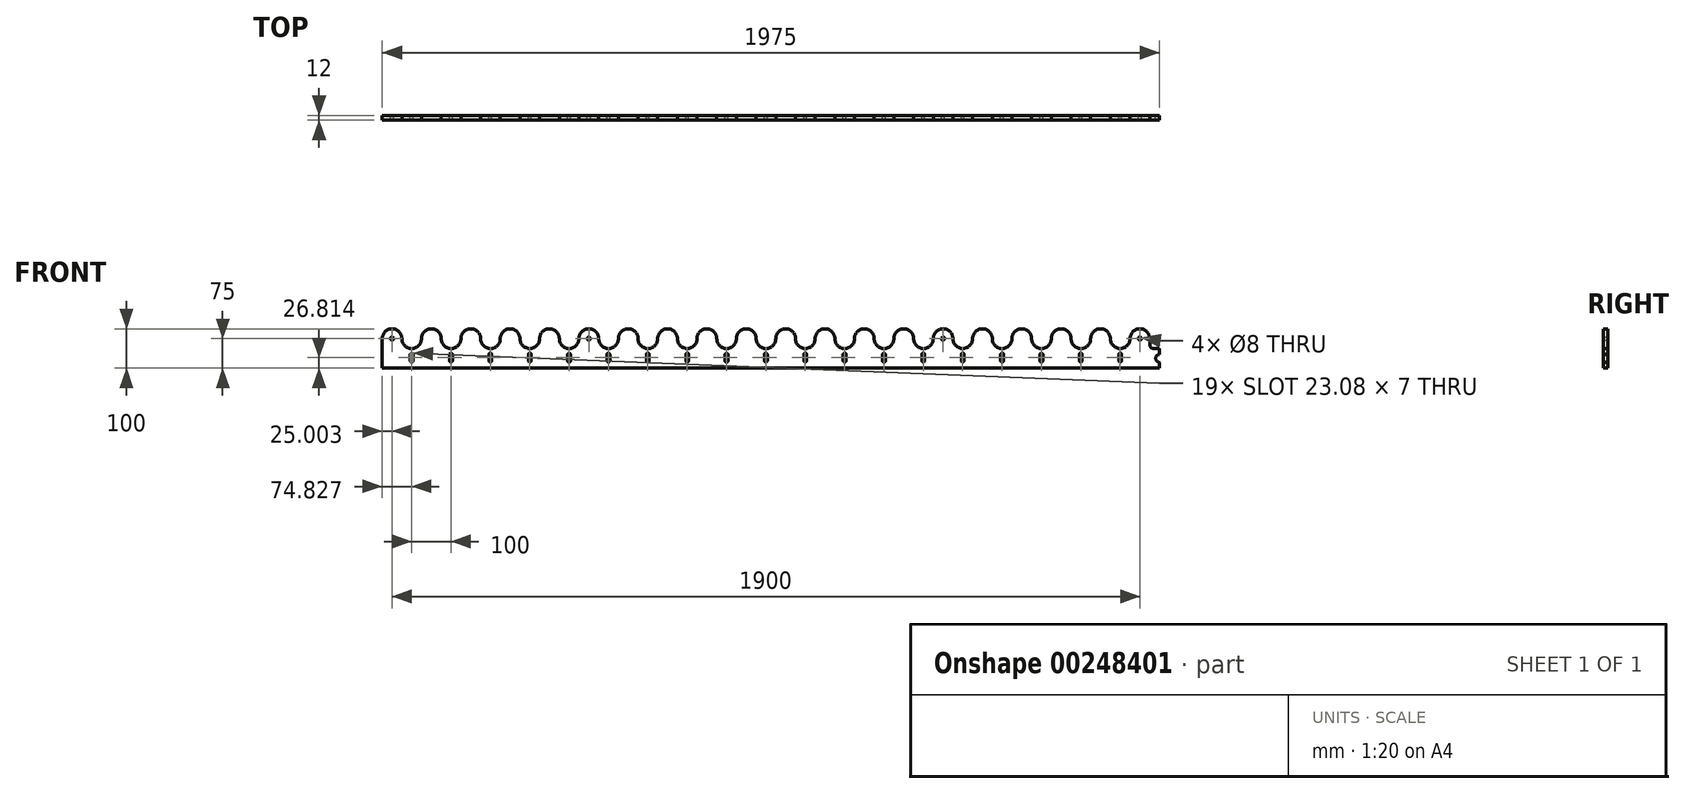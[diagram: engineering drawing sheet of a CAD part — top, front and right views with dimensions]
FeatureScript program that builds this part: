
annotation { "Feature Type Name" : "Feature", "Feature Type Description" : "" }
export const myFeature = defineFeature(function(context is Context, id is Id, definition is map)
    precondition{}
    {
        {
            var Q0;
            Q0=qCreatedBy(makeId("Front.planeOp"),FACE);
            var sketch = newSketch(context, id + "F0", { "sketchPlane" : qUnion([Q0])});
            skArc(sketch, "E0", {"start": v(19.37, 31.06) * mm, "mid": v(15.85, 34.56) * mm, "end": v(12.37, 31.03) * mm});
            skLineSegment(sketch, "E1", {"start": v(12.37, 31.03) * mm, "end": v(12.37, 14.95) * mm});
            skLineSegment(sketch, "E2", {"start": v(19.37, 31.06) * mm, "end": v(19.37, 14.98) * mm});
            skArc(sketch, "E3", {"start": v(19.37, 14.98) * mm, "mid": v(15.89, 11.48) * mm, "end": v(12.37, 14.95) * mm});
            skLineSegment(sketch, "E4.direction1", {"start": v(-61.28, 71.21) * mm, "end": v(88.44, 71.21) * mm, "construction": true});
            skLineSegment(sketch, "E5", {"start": v(-62.08, 71.21) * mm, "end": v(-78.8, 71.21) * mm, "construction": true});
            skLineSegment(sketch, "E6", {"start": v(15.87, 14.98) * mm, "end": v(16.2, 118.2) * mm, "construction": true});
            skArc(sketch, "E7", {"start": v(41.04, 71.21) * mm, "mid": v(16.04, 46.21) * mm, "end": v(-8.96, 71.21) * mm});
            skPoint(sketch, "E7.centerSnap0", {"position": v(13.58, 71.21) * mm});
            skArc(sketch, "E8", {"start": v(-8.96, 71.21) * mm, "mid": v(-33.96, 96.21) * mm, "end": v(-58.96, 71.21) * mm});
            skArc(sketch, "E9.1.0.0", {"start": v(91.04, 71.21) * mm, "mid": v(66.04, 96.21) * mm, "end": v(41.04, 71.21) * mm});
            skArc(sketch, "E9.1.0.1", {"start": v(141.04, 71.21) * mm, "mid": v(116.04, 46.21) * mm, "end": v(91.04, 71.21) * mm});
            skLineSegment(sketch, "E9.1.0.2", {"start": v(112.37, 31.03) * mm, "end": v(112.37, 14.95) * mm});
            skArc(sketch, "E9.1.0.3", {"start": v(119.37, 31.06) * mm, "mid": v(115.85, 34.56) * mm, "end": v(112.37, 31.03) * mm});
            skArc(sketch, "E9.1.0.4", {"start": v(119.37, 14.98) * mm, "mid": v(115.89, 11.48) * mm, "end": v(112.37, 14.95) * mm});
            skLineSegment(sketch, "E9.1.0.5", {"start": v(119.37, 31.06) * mm, "end": v(119.37, 14.98) * mm});
            skArc(sketch, "E9.2.0.0", {"start": v(191.04, 71.21) * mm, "mid": v(166.04, 96.21) * mm, "end": v(141.04, 71.21) * mm});
            skArc(sketch, "E9.2.0.1", {"start": v(241.04, 71.21) * mm, "mid": v(216.04, 46.21) * mm, "end": v(191.04, 71.21) * mm});
            skLineSegment(sketch, "E9.2.0.2", {"start": v(212.37, 31.03) * mm, "end": v(212.37, 14.95) * mm});
            skArc(sketch, "E9.2.0.3", {"start": v(219.37, 31.06) * mm, "mid": v(215.85, 34.56) * mm, "end": v(212.37, 31.03) * mm});
            skArc(sketch, "E9.2.0.4", {"start": v(219.37, 14.98) * mm, "mid": v(215.89, 11.48) * mm, "end": v(212.37, 14.95) * mm});
            skLineSegment(sketch, "E9.2.0.5", {"start": v(219.37, 31.06) * mm, "end": v(219.37, 14.98) * mm});
            skArc(sketch, "E9.3.0.0", {"start": v(291.04, 71.21) * mm, "mid": v(266.04, 96.21) * mm, "end": v(241.04, 71.21) * mm});
            skArc(sketch, "E9.3.0.1", {"start": v(341.04, 71.21) * mm, "mid": v(316.04, 46.21) * mm, "end": v(291.04, 71.21) * mm});
            skLineSegment(sketch, "E9.3.0.2", {"start": v(312.37, 31.03) * mm, "end": v(312.37, 14.95) * mm});
            skArc(sketch, "E9.3.0.3", {"start": v(319.37, 31.06) * mm, "mid": v(315.85, 34.56) * mm, "end": v(312.37, 31.03) * mm});
            skArc(sketch, "E9.3.0.4", {"start": v(319.37, 14.98) * mm, "mid": v(315.89, 11.48) * mm, "end": v(312.37, 14.95) * mm});
            skLineSegment(sketch, "E9.3.0.5", {"start": v(319.37, 31.06) * mm, "end": v(319.37, 14.98) * mm});
            skArc(sketch, "E9.4.0.0", {"start": v(391.04, 71.21) * mm, "mid": v(366.04, 96.21) * mm, "end": v(341.04, 71.21) * mm});
            skArc(sketch, "E9.4.0.1", {"start": v(441.04, 71.21) * mm, "mid": v(416.04, 46.21) * mm, "end": v(391.04, 71.21) * mm});
            skLineSegment(sketch, "E9.4.0.2", {"start": v(412.37, 31.03) * mm, "end": v(412.37, 14.95) * mm});
            skArc(sketch, "E9.4.0.3", {"start": v(419.37, 31.06) * mm, "mid": v(415.85, 34.56) * mm, "end": v(412.37, 31.03) * mm});
            skArc(sketch, "E9.4.0.4", {"start": v(419.37, 14.98) * mm, "mid": v(415.89, 11.48) * mm, "end": v(412.37, 14.95) * mm});
            skLineSegment(sketch, "E9.4.0.5", {"start": v(419.37, 31.06) * mm, "end": v(419.37, 14.98) * mm});
            skArc(sketch, "E9.5.0.0", {"start": v(491.04, 71.21) * mm, "mid": v(466.04, 96.21) * mm, "end": v(441.04, 71.21) * mm});
            skArc(sketch, "E9.5.0.1", {"start": v(541.04, 71.21) * mm, "mid": v(516.04, 46.21) * mm, "end": v(491.04, 71.21) * mm});
            skLineSegment(sketch, "E9.5.0.2", {"start": v(512.37, 31.03) * mm, "end": v(512.37, 14.95) * mm});
            skArc(sketch, "E9.5.0.3", {"start": v(519.37, 31.06) * mm, "mid": v(515.85, 34.56) * mm, "end": v(512.37, 31.03) * mm});
            skArc(sketch, "E9.5.0.4", {"start": v(519.37, 14.98) * mm, "mid": v(515.89, 11.48) * mm, "end": v(512.37, 14.95) * mm});
            skLineSegment(sketch, "E9.5.0.5", {"start": v(519.37, 31.06) * mm, "end": v(519.37, 14.98) * mm});
            skArc(sketch, "E9.6.0.0", {"start": v(591.04, 71.21) * mm, "mid": v(566.04, 96.21) * mm, "end": v(541.04, 71.21) * mm});
            skArc(sketch, "E9.6.0.1", {"start": v(641.04, 71.21) * mm, "mid": v(616.04, 46.21) * mm, "end": v(591.04, 71.21) * mm});
            skLineSegment(sketch, "E9.6.0.2", {"start": v(612.37, 31.03) * mm, "end": v(612.37, 14.95) * mm});
            skArc(sketch, "E9.6.0.3", {"start": v(619.37, 31.06) * mm, "mid": v(615.85, 34.56) * mm, "end": v(612.37, 31.03) * mm});
            skArc(sketch, "E9.6.0.4", {"start": v(619.37, 14.98) * mm, "mid": v(615.89, 11.48) * mm, "end": v(612.37, 14.95) * mm});
            skLineSegment(sketch, "E9.6.0.5", {"start": v(619.37, 31.06) * mm, "end": v(619.37, 14.98) * mm});
            skArc(sketch, "E9.7.0.0", {"start": v(691.04, 71.21) * mm, "mid": v(666.04, 96.21) * mm, "end": v(641.04, 71.21) * mm});
            skArc(sketch, "E9.7.0.1", {"start": v(741.04, 71.21) * mm, "mid": v(716.04, 46.21) * mm, "end": v(691.04, 71.21) * mm});
            skLineSegment(sketch, "E9.7.0.2", {"start": v(712.37, 31.03) * mm, "end": v(712.37, 14.95) * mm});
            skArc(sketch, "E9.7.0.3", {"start": v(719.37, 31.06) * mm, "mid": v(715.85, 34.56) * mm, "end": v(712.37, 31.03) * mm});
            skArc(sketch, "E9.7.0.4", {"start": v(719.37, 14.98) * mm, "mid": v(715.89, 11.48) * mm, "end": v(712.37, 14.95) * mm});
            skLineSegment(sketch, "E9.7.0.5", {"start": v(719.37, 31.06) * mm, "end": v(719.37, 14.98) * mm});
            skArc(sketch, "E9.8.0.0", {"start": v(791.04, 71.21) * mm, "mid": v(766.04, 96.21) * mm, "end": v(741.04, 71.21) * mm});
            skArc(sketch, "E9.8.0.1", {"start": v(841.04, 71.21) * mm, "mid": v(816.04, 46.21) * mm, "end": v(791.04, 71.21) * mm});
            skLineSegment(sketch, "E9.8.0.2", {"start": v(812.37, 31.03) * mm, "end": v(812.37, 14.95) * mm});
            skArc(sketch, "E9.8.0.3", {"start": v(819.37, 31.06) * mm, "mid": v(815.85, 34.56) * mm, "end": v(812.37, 31.03) * mm});
            skArc(sketch, "E9.8.0.4", {"start": v(819.37, 14.98) * mm, "mid": v(815.89, 11.48) * mm, "end": v(812.37, 14.95) * mm});
            skLineSegment(sketch, "E9.8.0.5", {"start": v(819.37, 31.06) * mm, "end": v(819.37, 14.98) * mm});
            skArc(sketch, "E9.9.0.0", {"start": v(891.04, 71.21) * mm, "mid": v(866.04, 96.21) * mm, "end": v(841.04, 71.21) * mm});
            skArc(sketch, "E9.9.0.1", {"start": v(941.04, 71.21) * mm, "mid": v(916.04, 46.21) * mm, "end": v(891.04, 71.21) * mm});
            skLineSegment(sketch, "E9.9.0.2", {"start": v(912.37, 31.03) * mm, "end": v(912.37, 14.95) * mm});
            skArc(sketch, "E9.9.0.3", {"start": v(919.37, 31.06) * mm, "mid": v(915.85, 34.56) * mm, "end": v(912.37, 31.03) * mm});
            skArc(sketch, "E9.9.0.4", {"start": v(919.37, 14.98) * mm, "mid": v(915.89, 11.48) * mm, "end": v(912.37, 14.95) * mm});
            skLineSegment(sketch, "E9.9.0.5", {"start": v(919.37, 31.06) * mm, "end": v(919.37, 14.98) * mm});
            skArc(sketch, "E9.10.0.0", {"start": v(991.04, 71.21) * mm, "mid": v(966.04, 96.21) * mm, "end": v(941.04, 71.21) * mm});
            skArc(sketch, "E9.10.0.1", {"start": v(1041.04, 71.21) * mm, "mid": v(1016.04, 46.21) * mm, "end": v(991.04, 71.21) * mm});
            skLineSegment(sketch, "E9.10.0.2", {"start": v(1012.37, 31.03) * mm, "end": v(1012.37, 14.95) * mm});
            skArc(sketch, "E9.10.0.3", {"start": v(1019.37, 31.06) * mm, "mid": v(1015.85, 34.56) * mm, "end": v(1012.37, 31.03) * mm});
            skArc(sketch, "E9.10.0.4", {"start": v(1019.37, 14.98) * mm, "mid": v(1015.89, 11.48) * mm, "end": v(1012.37, 14.95) * mm});
            skLineSegment(sketch, "E9.10.0.5", {"start": v(1019.37, 31.06) * mm, "end": v(1019.37, 14.98) * mm});
            skArc(sketch, "E9.11.0.0", {"start": v(1091.04, 71.21) * mm, "mid": v(1066.04, 96.21) * mm, "end": v(1041.04, 71.21) * mm});
            skArc(sketch, "E9.11.0.1", {"start": v(1141.04, 71.21) * mm, "mid": v(1116.04, 46.21) * mm, "end": v(1091.04, 71.21) * mm});
            skLineSegment(sketch, "E9.11.0.2", {"start": v(1112.37, 31.03) * mm, "end": v(1112.37, 14.95) * mm});
            skArc(sketch, "E9.11.0.3", {"start": v(1119.37, 31.06) * mm, "mid": v(1115.85, 34.56) * mm, "end": v(1112.37, 31.03) * mm});
            skArc(sketch, "E9.11.0.4", {"start": v(1119.37, 14.98) * mm, "mid": v(1115.89, 11.48) * mm, "end": v(1112.37, 14.95) * mm});
            skLineSegment(sketch, "E9.11.0.5", {"start": v(1119.37, 31.06) * mm, "end": v(1119.37, 14.98) * mm});
            skArc(sketch, "E9.12.0.0", {"start": v(1191.04, 71.21) * mm, "mid": v(1166.04, 96.21) * mm, "end": v(1141.04, 71.21) * mm});
            skArc(sketch, "E9.12.0.1", {"start": v(1241.04, 71.21) * mm, "mid": v(1216.04, 46.21) * mm, "end": v(1191.04, 71.21) * mm});
            skLineSegment(sketch, "E9.12.0.2", {"start": v(1212.37, 31.03) * mm, "end": v(1212.37, 14.95) * mm});
            skArc(sketch, "E9.12.0.3", {"start": v(1219.37, 31.06) * mm, "mid": v(1215.85, 34.56) * mm, "end": v(1212.37, 31.03) * mm});
            skArc(sketch, "E9.12.0.4", {"start": v(1219.37, 14.98) * mm, "mid": v(1215.89, 11.48) * mm, "end": v(1212.37, 14.95) * mm});
            skLineSegment(sketch, "E9.12.0.5", {"start": v(1219.37, 31.06) * mm, "end": v(1219.37, 14.98) * mm});
            skArc(sketch, "E9.13.0.0", {"start": v(1291.04, 71.21) * mm, "mid": v(1266.04, 96.21) * mm, "end": v(1241.04, 71.21) * mm});
            skArc(sketch, "E9.13.0.1", {"start": v(1341.04, 71.21) * mm, "mid": v(1316.04, 46.21) * mm, "end": v(1291.04, 71.21) * mm});
            skLineSegment(sketch, "E9.13.0.2", {"start": v(1312.37, 31.03) * mm, "end": v(1312.37, 14.95) * mm});
            skArc(sketch, "E9.13.0.3", {"start": v(1319.37, 31.06) * mm, "mid": v(1315.85, 34.56) * mm, "end": v(1312.37, 31.03) * mm});
            skArc(sketch, "E9.13.0.4", {"start": v(1319.37, 14.98) * mm, "mid": v(1315.89, 11.48) * mm, "end": v(1312.37, 14.95) * mm});
            skLineSegment(sketch, "E9.13.0.5", {"start": v(1319.37, 31.06) * mm, "end": v(1319.37, 14.98) * mm});
            skArc(sketch, "E9.14.0.0", {"start": v(1391.04, 71.21) * mm, "mid": v(1366.04, 96.21) * mm, "end": v(1341.04, 71.21) * mm});
            skArc(sketch, "E9.14.0.1", {"start": v(1441.04, 71.21) * mm, "mid": v(1416.04, 46.21) * mm, "end": v(1391.04, 71.21) * mm});
            skLineSegment(sketch, "E9.14.0.2", {"start": v(1412.37, 31.03) * mm, "end": v(1412.37, 14.95) * mm});
            skArc(sketch, "E9.14.0.3", {"start": v(1419.37, 31.06) * mm, "mid": v(1415.85, 34.56) * mm, "end": v(1412.37, 31.03) * mm});
            skArc(sketch, "E9.14.0.4", {"start": v(1419.37, 14.98) * mm, "mid": v(1415.89, 11.48) * mm, "end": v(1412.37, 14.95) * mm});
            skLineSegment(sketch, "E9.14.0.5", {"start": v(1419.37, 31.06) * mm, "end": v(1419.37, 14.98) * mm});
            skArc(sketch, "E9.15.0.0", {"start": v(1491.04, 71.21) * mm, "mid": v(1466.04, 96.21) * mm, "end": v(1441.04, 71.21) * mm});
            skArc(sketch, "E9.15.0.1", {"start": v(1541.04, 71.21) * mm, "mid": v(1516.04, 46.21) * mm, "end": v(1491.04, 71.21) * mm});
            skLineSegment(sketch, "E9.15.0.2", {"start": v(1512.37, 31.03) * mm, "end": v(1512.37, 14.95) * mm});
            skArc(sketch, "E9.15.0.3", {"start": v(1519.37, 31.06) * mm, "mid": v(1515.85, 34.56) * mm, "end": v(1512.37, 31.03) * mm});
            skArc(sketch, "E9.15.0.4", {"start": v(1519.37, 14.98) * mm, "mid": v(1515.89, 11.48) * mm, "end": v(1512.37, 14.95) * mm});
            skLineSegment(sketch, "E9.15.0.5", {"start": v(1519.37, 31.06) * mm, "end": v(1519.37, 14.98) * mm});
            skArc(sketch, "E9.16.0.0", {"start": v(1591.04, 71.21) * mm, "mid": v(1566.04, 96.21) * mm, "end": v(1541.04, 71.21) * mm});
            skArc(sketch, "E9.16.0.1", {"start": v(1641.04, 71.21) * mm, "mid": v(1616.04, 46.21) * mm, "end": v(1591.04, 71.21) * mm});
            skLineSegment(sketch, "E9.16.0.2", {"start": v(1612.37, 31.03) * mm, "end": v(1612.37, 14.95) * mm});
            skArc(sketch, "E9.16.0.3", {"start": v(1619.37, 31.06) * mm, "mid": v(1615.85, 34.56) * mm, "end": v(1612.37, 31.03) * mm});
            skArc(sketch, "E9.16.0.4", {"start": v(1619.37, 14.98) * mm, "mid": v(1615.89, 11.48) * mm, "end": v(1612.37, 14.95) * mm});
            skLineSegment(sketch, "E9.16.0.5", {"start": v(1619.37, 31.06) * mm, "end": v(1619.37, 14.98) * mm});
            skArc(sketch, "E9.17.0.0", {"start": v(1691.04, 71.21) * mm, "mid": v(1666.04, 96.21) * mm, "end": v(1641.04, 71.21) * mm});
            skArc(sketch, "E9.17.0.1", {"start": v(1741.04, 71.21) * mm, "mid": v(1716.04, 46.21) * mm, "end": v(1691.04, 71.21) * mm});
            skLineSegment(sketch, "E9.17.0.2", {"start": v(1712.37, 31.03) * mm, "end": v(1712.37, 14.95) * mm});
            skArc(sketch, "E9.17.0.3", {"start": v(1719.37, 31.06) * mm, "mid": v(1715.85, 34.56) * mm, "end": v(1712.37, 31.03) * mm});
            skArc(sketch, "E9.17.0.4", {"start": v(1719.37, 14.98) * mm, "mid": v(1715.89, 11.48) * mm, "end": v(1712.37, 14.95) * mm});
            skLineSegment(sketch, "E9.17.0.5", {"start": v(1719.37, 31.06) * mm, "end": v(1719.37, 14.98) * mm});
            skArc(sketch, "E9.18.0.0", {"start": v(1791.04, 71.21) * mm, "mid": v(1766.04, 96.21) * mm, "end": v(1741.04, 71.21) * mm});
            skArc(sketch, "E9.18.0.1", {"start": v(1841.04, 71.21) * mm, "mid": v(1816.04, 46.21) * mm, "end": v(1791.04, 71.21) * mm});
            skLineSegment(sketch, "E9.18.0.2", {"start": v(1812.37, 31.03) * mm, "end": v(1812.37, 14.95) * mm});
            skArc(sketch, "E9.18.0.3", {"start": v(1819.37, 31.06) * mm, "mid": v(1815.85, 34.56) * mm, "end": v(1812.37, 31.03) * mm});
            skArc(sketch, "E9.18.0.4", {"start": v(1819.37, 14.98) * mm, "mid": v(1815.89, 11.48) * mm, "end": v(1812.37, 14.95) * mm});
            skLineSegment(sketch, "E9.18.0.5", {"start": v(1819.37, 31.06) * mm, "end": v(1819.37, 14.98) * mm});
            skArc(sketch, "E9.19.0.0", {"start": v(1891.04, 71.21) * mm, "mid": v(1866.04, 96.21) * mm, "end": v(1841.04, 71.21) * mm});
            skLineSegment(sketch, "E9.direction1", {"start": v(-58.96, 71.21) * mm, "end": v(41.04, 71.21) * mm, "construction": true});
            skLineSegment(sketch, "E10", {"start": v(-58.96, 71.21) * mm, "end": v(-58.96, -3.79) * mm});
            skLineSegment(sketch, "E11", {"start": v(-58.96, -3.79) * mm, "end": v(1891.04, -3.79) * mm});
            skLineSegment(sketch, "E12", {"start": v(1891.04, 71.21) * mm, "end": v(1891.04, 56.46) * mm});
            skLineSegment(sketch, "E13", {"start": v(1901.04, 46.24) * mm, "end": v(1916.04, 46.24) * mm});
            skLineSegment(sketch, "E14", {"start": v(1891.04, -3.79) * mm, "end": v(1916.04, -3.79) * mm});
            skPoint(sketch, "E15.visualSharp", {"position": v(1891.04, 46.24) * mm});
            skArc(sketch, "E15.filletArc", {"start": v(1891.04, 56.23) * mm, "mid": v(1893.98, 49.16) * mm, "end": v(1901.04, 46.24) * mm});
            skLineSegment(sketch, "E16", {"start": v(1891.04, 56.46) * mm, "end": v(1891.04, 56.23) * mm});
            skLineSegment(sketch, "E17", {"start": v(1916.04, 46.24) * mm, "end": v(1916.04, 31.22) * mm});
            skLineSegment(sketch, "E18", {"start": v(1916.04, 11.22) * mm, "end": v(1916.04, -3.79) * mm});
            skArc(sketch, "E19", {"start": v(1916.04, 31.22) * mm, "mid": v(1906.04, 21.22) * mm, "end": v(1916.04, 11.22) * mm});
            skCircle(sketch, "E20", {"center": v(1866.04, 71.21) * mm, "radius": 4 * mm});
            skCircle(sketch, "E21.1.0.0", {"center": v(-33.96, 71.21) * mm, "radius": 4 * mm});
            skLineSegment(sketch, "E21.direction1", {"start": v(1866.04, 71.21) * mm, "end": v(-33.96, 71.21) * mm, "construction": true});
            skLineSegment(sketch, "E22.direction1", {"start": v(1866.04, 71.21) * mm, "end": v(1366.04, 71.21) * mm, "construction": true});
            skCircle(sketch, "E23.0.1.0", {"center": v(1366.04, 71.21) * mm, "radius": 4 * mm});
            skCircle(sketch, "E24.1.0.0", {"center": v(466.04, 71.21) * mm, "radius": 4 * mm});
            skLineSegment(sketch, "E24.direction1", {"start": v(1866.04, 71.21) * mm, "end": v(466.04, 71.21) * mm, "construction": true});
            skSolve(sketch);
        }
        {
            var Q0;
            Q0=makeQuery(id+"F0.imprint","IMPRINT",FACE,{"disambiguationData":[TD([[makeQuery(id+"F0.imprint","IMPRINT",EDGE,{"derivedFrom":sQuery(id+"F0.wireOp",EDGE,"E0")}),-1.0]])]});
            extrude(context, id + "F1", {"entities" : qUnion([Q0]), "depth" : 12 * mm});
        }
    });
